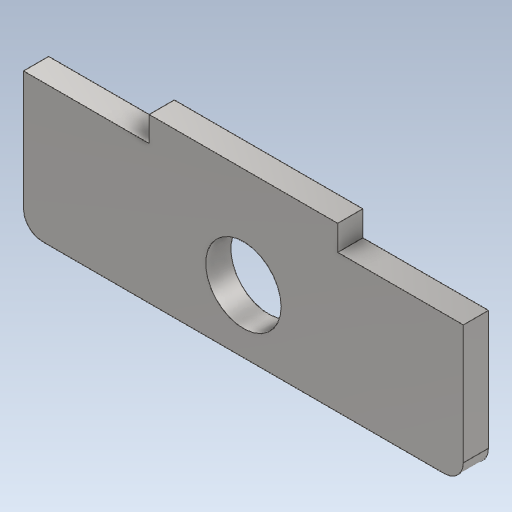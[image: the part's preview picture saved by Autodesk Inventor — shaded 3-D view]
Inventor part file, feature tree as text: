
AUTODESK INVENTOR PART (.ipt)
format: ipt  version: 2020 (Build 240168000, 168)  size: 169,472 bytes
history: native  units: mm
features: other x1, extrude x1
ambient origin geometry x8: Origin, YZ Plane, XZ Plane, XY Plane, X Axis, Y Axis, Z Axis, Center Point
bodies: Body1 (feature_tree)
feature tree (2):
  other  "實體1"
  extrude  "擠出1"  Depth=35.0mm
